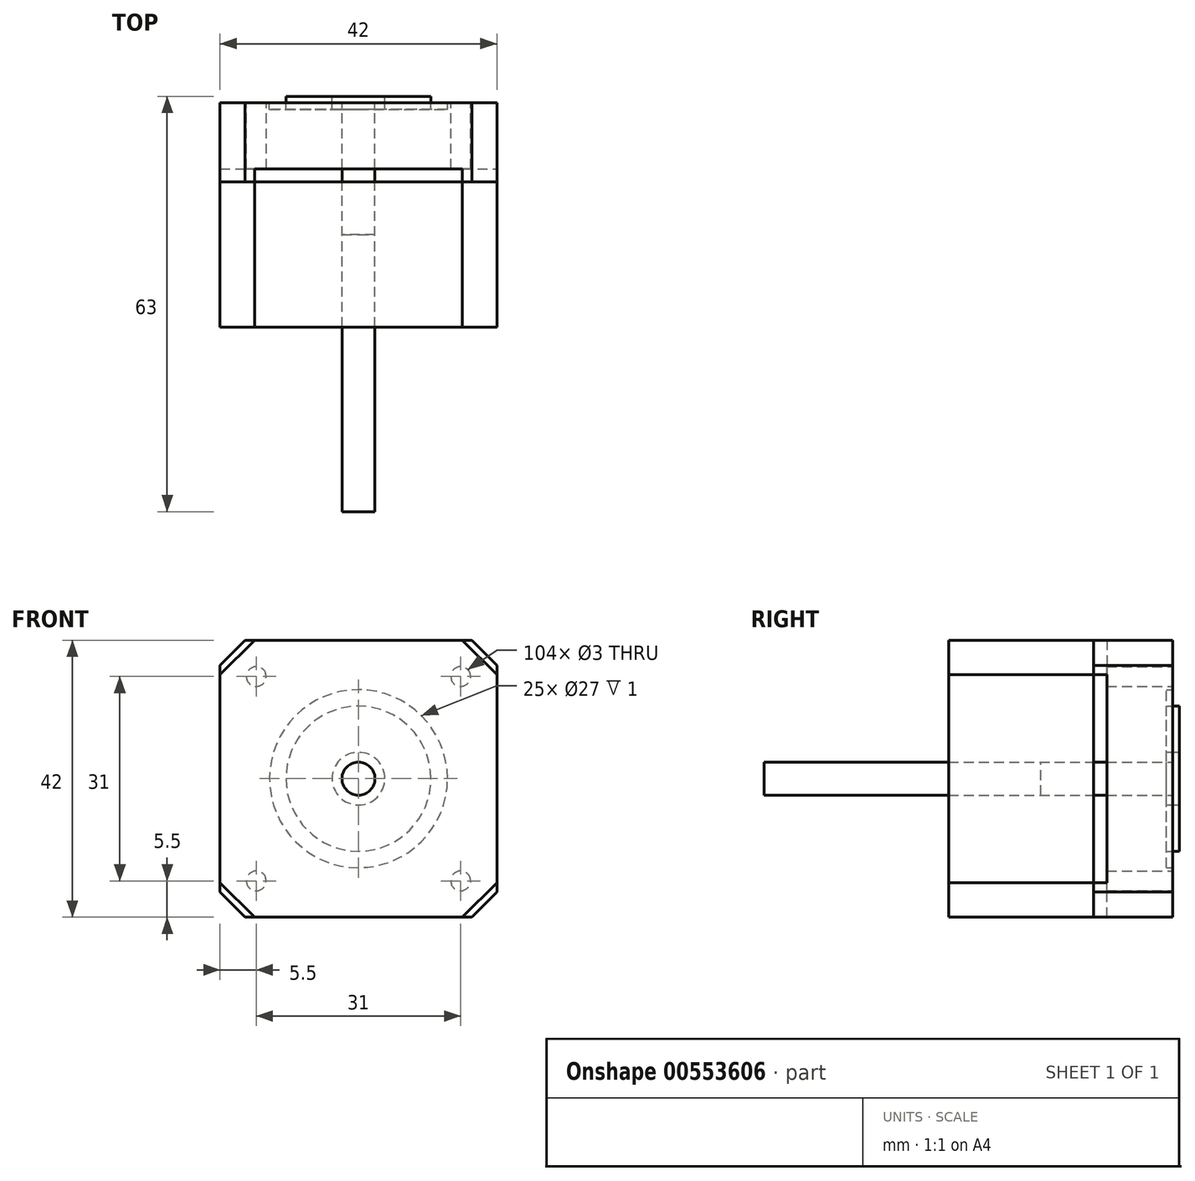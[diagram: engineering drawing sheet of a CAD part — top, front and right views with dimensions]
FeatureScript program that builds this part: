
annotation { "Feature Type Name" : "Feature", "Feature Type Description" : "" }
export const myFeature = defineFeature(function(context is Context, id is Id, definition is map)
    precondition{}
    {
        {
            var Q0;
            Q0=qCreatedBy(makeId("Front.planeOp"),FACE);
            var sketch = newSketch(context, id + "F0", { "sketchPlane" : qUnion([Q0])});
            skCircle(sketch, "E0", {"center": v(0, 0) * mm, "radius": 2.5 * mm});
            skCircle(sketch, "E1", {"center": v(0, 0) * mm, "radius": 11 * mm});
            skCircle(sketch, "E2", {"center": v(0, 0) * mm, "radius": 4 * mm});
            skCircle(sketch, "E3", {"center": v(0, 0) * mm, "radius": 13.5 * mm});
            skLineSegment(sketch, "E4.bottom", {"start": v(-17.18, 21) * mm, "end": v(17.18, 21) * mm});
            skLineSegment(sketch, "E4.top", {"start": v(-17.18, -21) * mm, "end": v(17.18, -21) * mm});
            skLineSegment(sketch, "E4.left", {"start": v(-21, 17.18) * mm, "end": v(-21, -17.18) * mm});
            skLineSegment(sketch, "E4.right", {"start": v(21, 17.18) * mm, "end": v(21, -17.18) * mm});
            skCircle(sketch, "E5", {"center": v(-15.5, 15.5) * mm, "radius": 1.5 * mm});
            skCircle(sketch, "E6", {"center": v(15.5, 15.5) * mm, "radius": 1.5 * mm});
            skCircle(sketch, "E7", {"center": v(15.5, -15.5) * mm, "radius": 1.5 * mm});
            skCircle(sketch, "E8", {"center": v(-15.5, -15.5) * mm, "radius": 1.5 * mm});
            skPoint(sketch, "E9.visualSharp", {"position": v(-21, 21) * mm});
            skPoint(sketch, "E10.visualSharp", {"position": v(21, 21) * mm});
            skPoint(sketch, "E11.visualSharp", {"position": v(21, -21) * mm});
            skPoint(sketch, "E12.visualSharp", {"position": v(-21, -21) * mm});
            skLineSegment(sketch, "E13", {"start": v(-21, -17.18) * mm, "end": v(-17.18, -21) * mm});
            skLineSegment(sketch, "E14", {"start": v(17.18, 21) * mm, "end": v(21, 17.18) * mm});
            skLineSegment(sketch, "E15", {"start": v(21, -17.18) * mm, "end": v(17.18, -21) * mm});
            skLineSegment(sketch, "E16", {"start": v(-21, 17.18) * mm, "end": v(-17.18, 21) * mm});
            skSolve(sketch);
        }
        {
            var Q0;
            Q0=makeQuery(id+"F0.imprint","IMPRINT",FACE,{"disambiguationData":[TD([[makeQuery(id+"F0.imprint","IMPRINT",EDGE,{"derivedFrom":sQuery(id+"F0.wireOp",EDGE,"E3")}),-1.0]])]});
            var Q1;
            Q1=makeQuery(id+"F0.imprint","IMPRINT",FACE,{"disambiguationData":[TD([[makeQuery(id+"F0.imprint","IMPRINT",EDGE,{"derivedFrom":sQuery(id+"F0.wireOp",EDGE,"E1")}),-1.0]])]});
            var Q2;
            Q2=makeQuery(id+"F0.imprint","IMPRINT",FACE,{"disambiguationData":[TD([[makeQuery(id+"F0.imprint","IMPRINT",EDGE,{"derivedFrom":sQuery(id+"F0.wireOp",EDGE,"E1")}),1.0]])]});
            var Q3;
            Q3=makeQuery(id+"F0.imprint","IMPRINT",FACE,{"disambiguationData":[TD([[makeQuery(id+"F0.imprint","IMPRINT",EDGE,{"derivedFrom":sQuery(id+"F0.wireOp",EDGE,"E0")}),1.0]])]});
            var Q4;
            Q4=makeQuery(id+"F0.imprint","IMPRINT",FACE,{"disambiguationData":[TD([[makeQuery(id+"F0.imprint","IMPRINT",EDGE,{"derivedFrom":sQuery(id+"F0.wireOp",EDGE,"E0")}),-1.0]])]});
            extrude(context, id + "F1", {"entities" : qUnion([Q0, Q1, Q2, Q3, Q4]), "depth" : 12 * mm, "offsetDistance" : 25 * mm});
        }
        {
            var Q0;
            Q0=makeQuery(id+"F0.imprint","IMPRINT",FACE,{"disambiguationData":[TD([[makeQuery(id+"F0.imprint","IMPRINT",EDGE,{"derivedFrom":sQuery(id+"F0.wireOp",EDGE,"E1")}),-1.0]])]});
            var Q1;
            Q1=makeQuery(id+"F0.imprint","IMPRINT",FACE,{"disambiguationData":[TD([[makeQuery(id+"F0.imprint","IMPRINT",EDGE,{"derivedFrom":sQuery(id+"F0.wireOp",EDGE,"E0")}),-1.0]])]});
            extrude(context, id + "F2", {"entities" : qUnion([Q0, Q1]), "operationType" : NewBodyOperationType.REMOVE, "depth" : 1 * mm, "offsetDistance" : 25 * mm});
        }
        {
            var Q0;
            Q0=makeQuery(id+"F0.imprint","IMPRINT",FACE,{"disambiguationData":[TD([[makeQuery(id+"F0.imprint","IMPRINT",EDGE,{"derivedFrom":sQuery(id+"F0.wireOp",EDGE,"E1")}),1.0]])]});
            extrude(context, id + "F3", {"entities" : qUnion([Q0]), "operationType" : NewBodyOperationType.ADD, "oppositeDirection" : true, "depth" : 1 * mm, "offsetDistance" : 25 * mm});
        }
        {
            var Q0;
            Q0=makeQuery(id+"F0.imprint","IMPRINT",FACE,{"disambiguationData":[TD([[makeQuery(id+"F0.imprint","IMPRINT",EDGE,{"derivedFrom":sQuery(id+"F0.wireOp",EDGE,"E0")}),1.0]])]});
            extrude(context, id + "F4", {"entities" : qUnion([Q0]), "operationType" : NewBodyOperationType.REMOVE, "depth" : 20 * mm, "offsetDistance" : 25 * mm});
        }
        {
            var Q0;
            Q0=makeQuery(id+"F1.opExtrude","CAP_FACE",FACE,{"disambiguationData":[OSD([sQuery(id+"F0.wireOp",EDGE,"E4.bottom"),sQuery(id+"F0.wireOp",EDGE,"E4.top"),sQuery(id+"F0.wireOp",EDGE,"E4.left"),sQuery(id+"F0.wireOp",EDGE,"E4.right"),sQuery(id+"F0.wireOp",EDGE,"E5"),sQuery(id+"F0.wireOp",EDGE,"E6"),sQuery(id+"F0.wireOp",EDGE,"E7"),sQuery(id+"F0.wireOp",EDGE,"E8"),sQuery(id+"F0.wireOp",EDGE,"E13"),sQuery(id+"F0.wireOp",EDGE,"E14"),sQuery(id+"F0.wireOp",EDGE,"E15"),sQuery(id+"F0.wireOp",EDGE,"E16")])],"isStart":false});
            var sketch = newSketch(context, id + "F5", { "sketchPlane" : qUnion([Q0])});
            skLineSegment(sketch, "E17.0", {"start": v(15.77, 21) * mm, "end": v(21, 15.77) * mm});
            skLineSegment(sketch, "E18.0", {"start": v(21, 15.77) * mm, "end": v(21, -15.77) * mm});
            skLineSegment(sketch, "E19", {"start": v(21, -15.77) * mm, "end": v(15.77, -21) * mm});
            skLineSegment(sketch, "E20", {"start": v(15.77, -21) * mm, "end": v(-15.77, -21) * mm});
            skLineSegment(sketch, "E21", {"start": v(-15.77, -21) * mm, "end": v(-21, -15.77) * mm});
            skLineSegment(sketch, "E22", {"start": v(-21, -15.77) * mm, "end": v(-21, 15.77) * mm});
            skLineSegment(sketch, "E23", {"start": v(-21, 15.77) * mm, "end": v(-15.77, 21) * mm});
            skLineSegment(sketch, "E24", {"start": v(-15.77, 21) * mm, "end": v(15.77, 21) * mm});
            skLineSegment(sketch, "E25", {"start": v(21, 0) * mm, "end": v(-21, 0) * mm, "construction": true});
            skLineSegment(sketch, "E26", {"start": v(0, 21) * mm, "end": v(0, -21) * mm, "construction": true});
            skCircle(sketch, "E27.0", {"center": v(0, 0) * mm, "radius": 2.5 * mm});
            skSolve(sketch);
        }
        {
            var Q0;
            Q0=qSketchRegion(id+"F5",true);
            extrude(context, id + "F6", {"entities" : qUnion([Q0]), "operationType" : NewBodyOperationType.REMOVE, "oppositeDirection" : true, "depth" : 2 * mm, "offsetDistance" : 25 * mm});
        }
        {
            var Q0;
            Q0=qSketchRegion(id+"F5",true);
            extrude(context, id + "F7", {"entities" : qUnion([Q0]), "depth" : 22 * mm, "offsetDistance" : 25 * mm, "hasSecondDirection" : true, "secondDirectionOppositeDirection" : true, "secondDirectionDepth" : 2 * mm});
        }
        {
            var Q0;
            Q0=makeQuery(id+"F0.imprint","IMPRINT",FACE,{"disambiguationData":[TD([[makeQuery(id+"F0.imprint","IMPRINT",EDGE,{"derivedFrom":sQuery(id+"F0.wireOp",EDGE,"E3")}),-1.0]])]});
            var Q1;
            Q1=makeQuery(id+"F0.imprint","IMPRINT",FACE,{"disambiguationData":[TD([[makeQuery(id+"F0.imprint","IMPRINT",EDGE,{"derivedFrom":sQuery(id+"F0.wireOp",EDGE,"E1")}),-1.0]])]});
            var Q2;
            Q2=makeQuery(id+"F0.imprint","IMPRINT",FACE,{"disambiguationData":[TD([[makeQuery(id+"F0.imprint","IMPRINT",EDGE,{"derivedFrom":sQuery(id+"F0.wireOp",EDGE,"E1")}),1.0]])]});
            var Q3;
            Q3=makeQuery(id+"F0.imprint","IMPRINT",FACE,{"disambiguationData":[TD([[makeQuery(id+"F0.imprint","IMPRINT",EDGE,{"derivedFrom":sQuery(id+"F0.wireOp",EDGE,"E0")}),-1.0]])]});
            extrude(context, id + "F8", {"entities" : qUnion([Q0, Q1, Q2, Q3]), "depth" : 12 * mm, "offsetDistance" : 25 * mm});
        }
        {
            var Q0;
            Q0=makeQuery(id+"F0.imprint","IMPRINT",FACE,{"disambiguationData":[TD([[makeQuery(id+"F0.imprint","IMPRINT",EDGE,{"derivedFrom":sQuery(id+"F0.wireOp",EDGE,"E1")}),1.0]])]});
            extrude(context, id + "F9", {"entities" : qUnion([Q0]), "operationType" : NewBodyOperationType.REMOVE, "depth" : 1 * mm, "offsetDistance" : 25 * mm});
        }
        {
            var Q0;
            Q0=qSketchRegion(id+"F5",true);
            extrude(context, id + "F10", {"entities" : qUnion([Q0]), "operationType" : NewBodyOperationType.REMOVE, "oppositeDirection" : true, "depth" : 2 * mm, "offsetDistance" : 25 * mm});
        }
        {
            var Q0;
            Q0=makeQuery(id+"F0.imprint","IMPRINT",FACE,{"disambiguationData":[TD([[makeQuery(id+"F0.imprint","IMPRINT",EDGE,{"derivedFrom":sQuery(id+"F0.wireOp",EDGE,"E0")}),1.0]])]});
            extrude(context, id + "F11", {"entities" : qUnion([Q0]), "depth" : 62 * mm, "offsetDistance" : 25 * mm});
        }
    });
